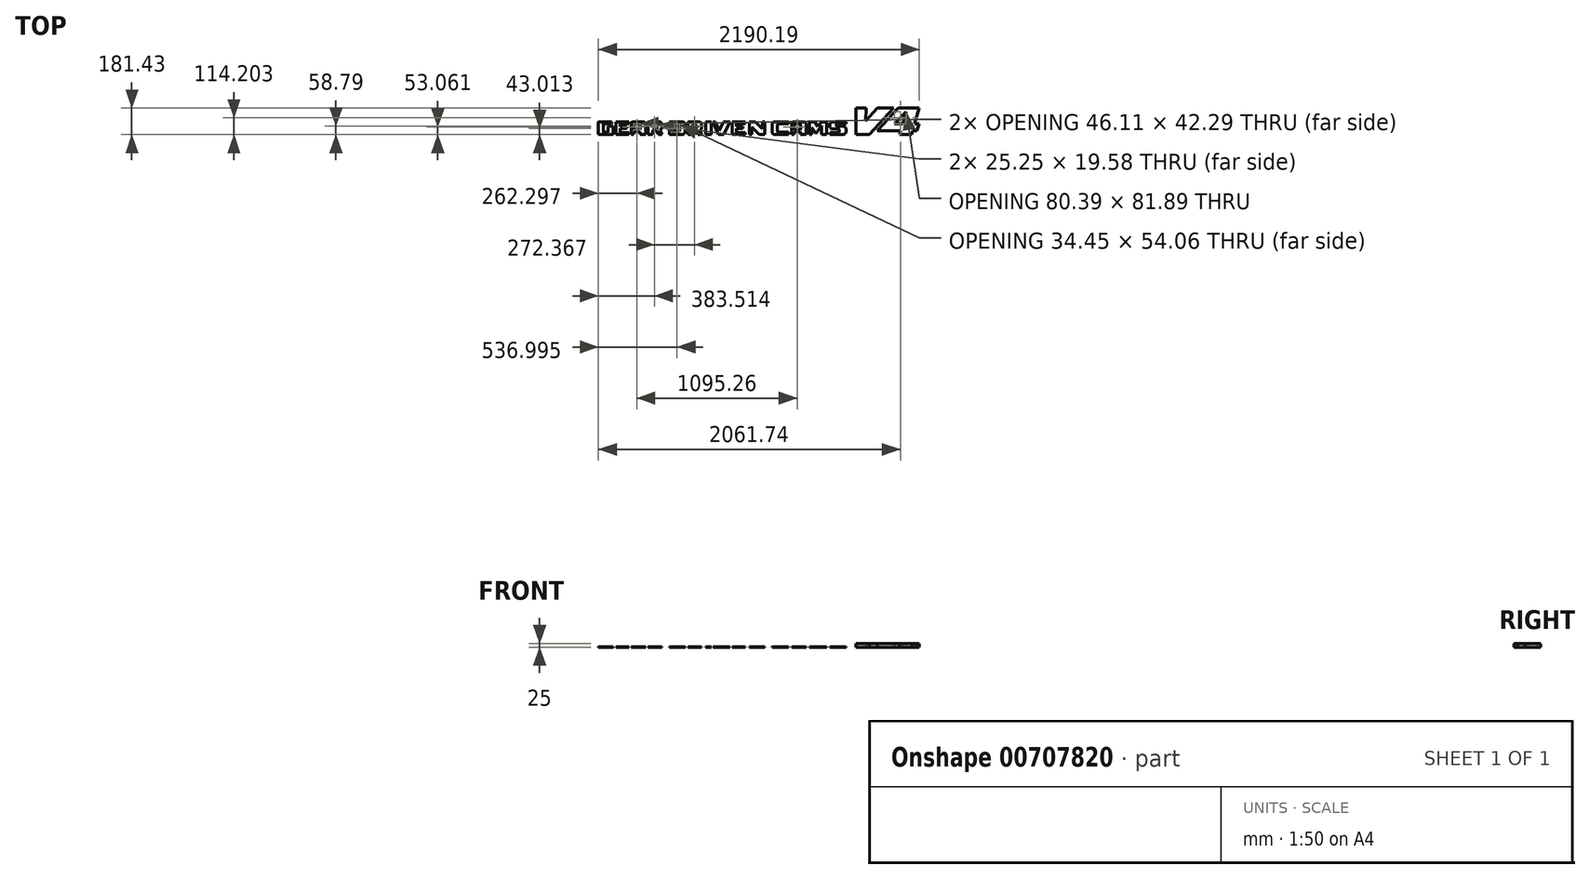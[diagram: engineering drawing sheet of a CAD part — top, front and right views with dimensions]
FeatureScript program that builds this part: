
annotation { "Feature Type Name" : "Feature", "Feature Type Description" : "" }
export const myFeature = defineFeature(function(context is Context, id is Id, definition is map)
    precondition{}
    {
        {
            var Q0;
            Q0=qCreatedBy(makeId("Top.planeOp"),FACE);
            var sketch = newSketch(context, id + "F0", { "sketchPlane" : qUnion([Q0])});
            skLineSegment(sketch, "E0", {"start": v(710.09, 395.52) * mm, "end": v(780, 395.52) * mm});
            skLineSegment(sketch, "E1", {"start": v(710.56, 214.09) * mm, "end": v(803.68, 214.09) * mm});
            skLineSegment(sketch, "E2", {"start": v(1092.02, 214.09) * mm, "end": v(1099.14, 239.05) * mm});
            skLineSegment(sketch, "E3", {"start": v(710.09, 395.52) * mm, "end": v(710.56, 214.09) * mm});
            skLineSegment(sketch, "E4", {"start": v(780, 395.52) * mm, "end": v(779.12, 307.5) * mm});
            skLineSegment(sketch, "E5", {"start": v(779.12, 307.5) * mm, "end": v(856.18, 395.52) * mm});
            skLineSegment(sketch, "E6", {"start": v(970.25, 395.52) * mm, "end": v(803.68, 214.09) * mm});
            skLineSegment(sketch, "E7", {"start": v(1000.95, 395.52) * mm, "end": v(857.3, 239.05) * mm});
            skLineSegment(sketch, "E8", {"start": v(1009.44, 214.09) * mm, "end": v(1016.85, 239.05) * mm});
            skLineSegment(sketch, "E9", {"start": v(975.1, 287.35) * mm, "end": v(1031.19, 287.35) * mm});
            skLineSegment(sketch, "E10", {"start": v(1142.08, 287.35) * mm, "end": v(1128.3, 239.05) * mm});
            skLineSegment(sketch, "E11", {"start": v(1128.3, 239.05) * mm, "end": v(1099.14, 239.05) * mm});
            skLineSegment(sketch, "E12.trimOffspring", {"start": v(856.18, 395.52) * mm, "end": v(970.25, 395.52) * mm});
            skLineSegment(sketch, "E13.trimOffspring", {"start": v(1009.44, 214.09) * mm, "end": v(1092.02, 214.09) * mm});
            skLineSegment(sketch, "E14.trimOffspring", {"start": v(1016.85, 239.05) * mm, "end": v(857.3, 239.05) * mm});
            skLineSegment(sketch, "E15.trimOffspring", {"start": v(1112.9, 287.35) * mm, "end": v(1142.08, 287.35) * mm});
            skLineSegment(sketch, "E16.trimOffspring", {"start": v(1031.19, 287.35) * mm, "end": v(1055.5, 369.24) * mm});
            skLineSegment(sketch, "E17.trimOffspring", {"start": v(1055.5, 369.24) * mm, "end": v(975.1, 287.35) * mm});
            skLineSegment(sketch, "E18.trimOffspring", {"start": v(1000.95, 395.52) * mm, "end": v(1151.02, 395.52) * mm});
            skLineSegment(sketch, "E19.trimOffspring", {"start": v(1112.9, 287.35) * mm, "end": v(1143.75, 395.52) * mm});
            skSolve(sketch);
        }
        {
            var Q0;
            Q0=makeQuery(id+"F0.imprint","IMPRINT",FACE,{"disambiguationData":[TD([[makeQuery(id+"F0.imprint","IMPRINT",EDGE,{"derivedFrom":sQuery(id+"F0.wireOp",EDGE,"E0")}),-1.0]])]});
            var Q1;
            Q1=makeQuery(id+"F0.imprint","IMPRINT",FACE,{"disambiguationData":[TD([[makeQuery(id+"F0.imprint","IMPRINT",EDGE,{"derivedFrom":sQuery(id+"F0.wireOp",EDGE,"E2")}),1.0]])]});
            extrude(context, id + "F1", {"entities" : qUnion([Q0, Q1]), "depth" : 25 * mm, "offsetDistance" : 25 * mm});
        }
        {
            var Q0;
            Q0=qCreatedBy(makeId("Top.planeOp"),FACE);
            var sketch = newSketch(context, id + "F2", { "sketchPlane" : qUnion([Q0])});
            skLineSegment(sketch, "E20", {"start": v(-1041.44, 302.21) * mm, "end": v(-955.7, 302.21) * mm});
            skLineSegment(sketch, "E21.0", {"start": v(-1041.44, 214.35) * mm, "end": v(-949.8, 214.35) * mm});
            skLineSegment(sketch, "E22", {"start": v(-1046.44, 219.35) * mm, "end": v(-1046.44, 297.21) * mm});
            skLineSegment(sketch, "E23", {"start": v(-1013.6, 236.44) * mm, "end": v(-1013.6, 283.53) * mm});
            skLineSegment(sketch, "E24", {"start": v(-979.78, 236.44) * mm, "end": v(-979.78, 270.86) * mm});
            skLineSegment(sketch, "E25", {"start": v(-944.8, 219.35) * mm, "end": v(-944.8, 270.86) * mm});
            skLineSegment(sketch, "E26", {"start": v(-925.97, 214.35) * mm, "end": v(-925.97, 302.21) * mm});
            skLineSegment(sketch, "E27", {"start": v(-897.14, 228.92) * mm, "end": v(-897.14, 255.43) * mm});
            skLineSegment(sketch, "E28", {"start": v(-852.65, 255.43) * mm, "end": v(-852.65, 269.68) * mm});
            skLineSegment(sketch, "E29", {"start": v(-838.3, 214.35) * mm, "end": v(-838.3, 228.92) * mm});
            skLineSegment(sketch, "E30", {"start": v(-822.44, 214.35) * mm, "end": v(-822.44, 289.99) * mm});
            skLineSegment(sketch, "E31", {"start": v(-807.2, 214.35) * mm, "end": v(-807.2, 233.5) * mm});
            skLineSegment(sketch, "E32", {"start": v(-761.09, 214.21) * mm, "end": v(-761.09, 233.5) * mm});
            skLineSegment(sketch, "E33", {"start": v(-723.62, 214.35) * mm, "end": v(-723.62, 283.68) * mm});
            skLineSegment(sketch, "E34", {"start": v(-706.35, 214.35) * mm, "end": v(-706.35, 302.21) * mm});
            skLineSegment(sketch, "E35", {"start": v(-675.55, 214.35) * mm, "end": v(-675.55, 243.5) * mm});
            skLineSegment(sketch, "E36", {"start": v(-613.77, 264.76) * mm, "end": v(-613.77, 284.75) * mm});
            skLineSegment(sketch, "E37", {"start": v(-1008.6, 231.44) * mm, "end": v(-984.78, 231.44) * mm});
            skLineSegment(sketch, "E38", {"start": v(-955.7, 288.53) * mm, "end": v(-955.7, 302.21) * mm});
            skLineSegment(sketch, "E39", {"start": v(-955.7, 288.53) * mm, "end": v(-1008.6, 288.53) * mm});
            skLineSegment(sketch, "E40", {"start": v(-944.8, 270.86) * mm, "end": v(-979.78, 270.86) * mm});
            skLineSegment(sketch, "E41", {"start": v(-838.3, 287.94) * mm, "end": v(-897.14, 287.94) * mm});
            skLineSegment(sketch, "E42", {"start": v(-852.65, 269.68) * mm, "end": v(-897.14, 269.68) * mm});
            skLineSegment(sketch, "E43", {"start": v(-852.65, 255.43) * mm, "end": v(-897.14, 255.43) * mm});
            skLineSegment(sketch, "E44", {"start": v(-838.3, 228.92) * mm, "end": v(-897.14, 228.92) * mm});
            skLineSegment(sketch, "E45.trimOffspring", {"start": v(-897.14, 269.68) * mm, "end": v(-897.14, 287.94) * mm});
            skLineSegment(sketch, "E46.trimOffspring", {"start": v(-838.3, 287.94) * mm, "end": v(-838.3, 302.21) * mm});
            skLineSegment(sketch, "E47", {"start": v(-761.09, 233.5) * mm, "end": v(-807.2, 233.5) * mm});
            skLineSegment(sketch, "E48", {"start": v(-807.2, 246) * mm, "end": v(-761.09, 246) * mm});
            skLineSegment(sketch, "E49", {"start": v(-797.2, 288.3) * mm, "end": v(-771.09, 288.3) * mm});
            skLineSegment(sketch, "E50.trimOffspring", {"start": v(-761.09, 246) * mm, "end": v(-761.09, 278.3) * mm});
            skLineSegment(sketch, "E51.trimOffspring", {"start": v(-807.2, 246) * mm, "end": v(-807.2, 278.3) * mm});
            skLineSegment(sketch, "E52", {"start": v(-675.55, 243.5) * mm, "end": v(-650.3, 243.5) * mm});
            skLineSegment(sketch, "E53", {"start": v(-650.3, 243.5) * mm, "end": v(-638.77, 214.35) * mm});
            skLineSegment(sketch, "E54.bottom", {"start": v(-675.55, 263.09) * mm, "end": v(-650.3, 263.09) * mm});
            skLineSegment(sketch, "E54.top", {"start": v(-675.55, 282.67) * mm, "end": v(-650.3, 282.67) * mm});
            skLineSegment(sketch, "E54.left", {"start": v(-675.55, 263.09) * mm, "end": v(-675.55, 282.67) * mm});
            skLineSegment(sketch, "E54.right", {"start": v(-650.3, 263.09) * mm, "end": v(-650.3, 282.67) * mm});
            skLineSegment(sketch, "E55", {"start": v(-613.77, 214.35) * mm, "end": v(-625.3, 243.5) * mm});
            skArc(sketch, "E56", {"start": v(-613.77, 284.75) * mm, "mid": v(-620.33, 297.33) * mm, "end": v(-633.64, 302.21) * mm});
            skArc(sketch, "E57", {"start": v(-625.3, 243.5) * mm, "mid": v(-616.69, 252.58) * mm, "end": v(-613.77, 264.76) * mm});
            skPoint(sketch, "E58.visualSharp", {"position": v(-1013.6, 231.44) * mm});
            skArc(sketch, "E58.filletArc", {"start": v(-1013.6, 236.44) * mm, "mid": v(-1012.14, 232.9) * mm, "end": v(-1008.6, 231.44) * mm});
            skPoint(sketch, "E59.visualSharp", {"position": v(-979.78, 231.44) * mm});
            skArc(sketch, "E59.filletArc", {"start": v(-984.78, 231.44) * mm, "mid": v(-981.25, 232.9) * mm, "end": v(-979.78, 236.44) * mm});
            skPoint(sketch, "E60.visualSharp", {"position": v(-1013.6, 288.53) * mm});
            skArc(sketch, "E60.filletArc", {"start": v(-1008.6, 288.53) * mm, "mid": v(-1012.14, 287.07) * mm, "end": v(-1013.6, 283.53) * mm});
            skLineSegment(sketch, "E61.trimOffspring", {"start": v(-925.97, 302.21) * mm, "end": v(-838.3, 302.21) * mm});
            skLineSegment(sketch, "E62.trimOffspring", {"start": v(-925.97, 214.35) * mm, "end": v(-838.3, 214.35) * mm});
            skPoint(sketch, "E63.visualSharp", {"position": v(-1046.44, 302.21) * mm});
            skArc(sketch, "E63.filletArc", {"start": v(-1041.44, 302.21) * mm, "mid": v(-1044.97, 300.75) * mm, "end": v(-1046.44, 297.21) * mm});
            skPoint(sketch, "E64.visualSharp", {"position": v(-1046.44, 214.35) * mm});
            skArc(sketch, "E64.filletArc", {"start": v(-1046.44, 219.35) * mm, "mid": v(-1044.97, 215.8) * mm, "end": v(-1041.44, 214.35) * mm});
            skPoint(sketch, "E65.visualSharp", {"position": v(-944.8, 214.35) * mm});
            skArc(sketch, "E65.filletArc", {"start": v(-949.8, 214.35) * mm, "mid": v(-946.26, 215.8) * mm, "end": v(-944.8, 219.35) * mm});
            skLineSegment(sketch, "E66.trimOffspring", {"start": v(-807.96, 302.21) * mm, "end": v(-742.83, 302.21) * mm});
            skLineSegment(sketch, "E67.trimOffspring", {"start": v(-822.44, 214.35) * mm, "end": v(-807.2, 214.35) * mm});
            skLineSegment(sketch, "E68.trimOffspring", {"start": v(-706.35, 214.35) * mm, "end": v(-675.55, 214.35) * mm});
            skLineSegment(sketch, "E69.trimOffspring", {"start": v(-706.35, 302.21) * mm, "end": v(-632.95, 302.21) * mm});
            skLineSegment(sketch, "E70.trimOffspring", {"start": v(-638.77, 214.35) * mm, "end": v(-613.77, 214.35) * mm});
            skArc(sketch, "E71", {"start": v(-807.96, 302.21) * mm, "mid": v(-817.4, 298.71) * mm, "end": v(-822.44, 289.99) * mm});
            skArc(sketch, "E72", {"start": v(-723.62, 283.68) * mm, "mid": v(-729.82, 296.96) * mm, "end": v(-743.5, 302.21) * mm});
            skPoint(sketch, "E73.visualSharp", {"position": v(-807.2, 288.3) * mm});
            skArc(sketch, "E73.filletArc", {"start": v(-797.2, 288.3) * mm, "mid": v(-804.27, 285.37) * mm, "end": v(-807.2, 278.3) * mm});
            skPoint(sketch, "E74.visualSharp", {"position": v(-761.09, 288.3) * mm});
            skArc(sketch, "E74.filletArc", {"start": v(-761.09, 278.3) * mm, "mid": v(-764.02, 285.37) * mm, "end": v(-771.09, 288.3) * mm});
            skLineSegment(sketch, "E75.trimOffspring", {"start": v(-761.09, 214.35) * mm, "end": v(-723.62, 214.35) * mm});
            skLineSegment(sketch, "E76", {"start": v(-562.57, 214.35) * mm, "end": v(-562.57, 302.21) * mm});
            skLineSegment(sketch, "E77", {"start": v(-526.67, 230.07) * mm, "end": v(-526.67, 284.13) * mm});
            skLineSegment(sketch, "E78", {"start": v(-492.22, 242.07) * mm, "end": v(-492.22, 272.13) * mm});
            skLineSegment(sketch, "E79", {"start": v(-454.92, 233.35) * mm, "end": v(-454.92, 283.21) * mm});
            skLineSegment(sketch, "E80", {"start": v(-526.67, 230.07) * mm, "end": v(-504.22, 230.07) * mm});
            skLineSegment(sketch, "E81", {"start": v(-526.67, 284.13) * mm, "end": v(-504.22, 284.13) * mm});
            skLineSegment(sketch, "E82", {"start": v(-433.98, 214.35) * mm, "end": v(-433.98, 302.21) * mm});
            skLineSegment(sketch, "E83", {"start": v(-403.18, 214.35) * mm, "end": v(-403.18, 243.5) * mm});
            skLineSegment(sketch, "E84", {"start": v(-341.4, 264.76) * mm, "end": v(-341.4, 284.75) * mm});
            skLineSegment(sketch, "E85", {"start": v(-403.18, 243.5) * mm, "end": v(-377.94, 243.5) * mm});
            skLineSegment(sketch, "E86", {"start": v(-377.94, 243.5) * mm, "end": v(-366.4, 214.35) * mm});
            skLineSegment(sketch, "E87.bottom", {"start": v(-403.18, 263.09) * mm, "end": v(-377.94, 263.09) * mm});
            skLineSegment(sketch, "E87.top", {"start": v(-403.18, 282.67) * mm, "end": v(-377.94, 282.67) * mm});
            skLineSegment(sketch, "E87.left", {"start": v(-403.18, 263.09) * mm, "end": v(-403.18, 282.67) * mm});
            skLineSegment(sketch, "E87.right", {"start": v(-377.94, 263.09) * mm, "end": v(-377.94, 282.67) * mm});
            skLineSegment(sketch, "E88", {"start": v(-341.4, 214.35) * mm, "end": v(-352.94, 243.5) * mm});
            skArc(sketch, "E89", {"start": v(-341.4, 284.75) * mm, "mid": v(-347.96, 297.33) * mm, "end": v(-361.27, 302.21) * mm});
            skArc(sketch, "E90", {"start": v(-352.94, 243.5) * mm, "mid": v(-344.32, 252.58) * mm, "end": v(-341.4, 264.76) * mm});
            skLineSegment(sketch, "E91.trimOffspring", {"start": v(-433.98, 214.35) * mm, "end": v(-403.18, 214.35) * mm});
            skLineSegment(sketch, "E92", {"start": v(-313.98, 214.35) * mm, "end": v(-313.98, 302.21) * mm});
            skLineSegment(sketch, "E93", {"start": v(-276.13, 214.35) * mm, "end": v(-276.13, 302.21) * mm});
            skLineSegment(sketch, "E94", {"start": v(-264.3, 302.21) * mm, "end": v(-229.62, 214.35) * mm});
            skLineSegment(sketch, "E95", {"start": v(-245.97, 302.21) * mm, "end": v(-221.92, 241.29) * mm});
            skLineSegment(sketch, "E96", {"start": v(-221.92, 241.29) * mm, "end": v(-192.95, 302.21) * mm});
            skLineSegment(sketch, "E97", {"start": v(-189.49, 214.35) * mm, "end": v(-147.71, 302.21) * mm});
            skLineSegment(sketch, "E98", {"start": v(-132.31, 214.35) * mm, "end": v(-132.31, 302.21) * mm});
            skLineSegment(sketch, "E99", {"start": v(-103.49, 228.92) * mm, "end": v(-103.49, 255.43) * mm});
            skLineSegment(sketch, "E100", {"start": v(-59, 255.43) * mm, "end": v(-59, 269.68) * mm});
            skLineSegment(sketch, "E101", {"start": v(-44.64, 214.35) * mm, "end": v(-44.64, 228.92) * mm});
            skLineSegment(sketch, "E102", {"start": v(-44.64, 287.94) * mm, "end": v(-103.49, 287.94) * mm});
            skLineSegment(sketch, "E103", {"start": v(-59, 269.68) * mm, "end": v(-103.49, 269.68) * mm});
            skLineSegment(sketch, "E104", {"start": v(-59, 255.43) * mm, "end": v(-103.49, 255.43) * mm});
            skLineSegment(sketch, "E105", {"start": v(-44.64, 228.92) * mm, "end": v(-103.49, 228.92) * mm});
            skLineSegment(sketch, "E106.trimOffspring", {"start": v(-103.49, 269.68) * mm, "end": v(-103.49, 287.94) * mm});
            skLineSegment(sketch, "E107.trimOffspring", {"start": v(-44.64, 287.94) * mm, "end": v(-44.64, 302.21) * mm});
            skLineSegment(sketch, "E108.trimOffspring", {"start": v(-132.31, 302.21) * mm, "end": v(-44.64, 302.21) * mm});
            skLineSegment(sketch, "E109.trimOffspring", {"start": v(-132.31, 214.35) * mm, "end": v(-44.64, 214.35) * mm});
            skLineSegment(sketch, "E110", {"start": v(-17, 214.35) * mm, "end": v(-17, 302.21) * mm});
            skLineSegment(sketch, "E111", {"start": v(0, 214.35) * mm, "end": v(0, 266.45) * mm});
            skLineSegment(sketch, "E112", {"start": v(72.6, 253.49) * mm, "end": v(72.6, 302.21) * mm});
            skLineSegment(sketch, "E113", {"start": v(89.95, 214.35) * mm, "end": v(89.95, 302.21) * mm});
            skLineSegment(sketch, "E114", {"start": v(25.32, 302.21) * mm, "end": v(72.6, 253.49) * mm});
            skLineSegment(sketch, "E115", {"start": v(0, 266.45) * mm, "end": v(50.55, 214.35) * mm});
            skLineSegment(sketch, "E116", {"start": v(138.96, 233.35) * mm, "end": v(138.96, 283.21) * mm});
            skLineSegment(sketch, "E117", {"start": v(174.7, 241.36) * mm, "end": v(174.7, 274.7) * mm});
            skLineSegment(sketch, "E118", {"start": v(252.03, 214.35) * mm, "end": v(252.03, 229.36) * mm});
            skLineSegment(sketch, "E119", {"start": v(392.53, 214.35) * mm, "end": v(392.53, 302.21) * mm});
            skLineSegment(sketch, "E120", {"start": v(410.35, 214.35) * mm, "end": v(410.35, 262.98) * mm});
            skLineSegment(sketch, "E121", {"start": v(475.18, 214.35) * mm, "end": v(475.49, 273.97) * mm});
            skLineSegment(sketch, "E122", {"start": v(510.56, 214.35) * mm, "end": v(510.56, 302.21) * mm});
            skLineSegment(sketch, "E123", {"start": v(533.94, 214.35) * mm, "end": v(533.94, 228.78) * mm});
            skLineSegment(sketch, "E124", {"start": v(643.75, 233.35) * mm, "end": v(643.75, 251.93) * mm});
            skLineSegment(sketch, "E125", {"start": v(272.81, 214.35) * mm, "end": v(272.81, 289.99) * mm});
            skLineSegment(sketch, "E126", {"start": v(288.06, 214.35) * mm, "end": v(288.06, 233.5) * mm});
            skLineSegment(sketch, "E127", {"start": v(334.17, 214.21) * mm, "end": v(334.17, 233.5) * mm});
            skLineSegment(sketch, "E128", {"start": v(371.64, 214.35) * mm, "end": v(371.64, 283.68) * mm});
            skLineSegment(sketch, "E129", {"start": v(334.17, 233.5) * mm, "end": v(288.06, 233.5) * mm});
            skLineSegment(sketch, "E130", {"start": v(288.06, 246) * mm, "end": v(334.17, 246) * mm});
            skLineSegment(sketch, "E131", {"start": v(298.06, 288.3) * mm, "end": v(324.17, 288.3) * mm});
            skLineSegment(sketch, "E132.trimOffspring", {"start": v(334.17, 246) * mm, "end": v(334.17, 278.3) * mm});
            skLineSegment(sketch, "E133.trimOffspring", {"start": v(288.06, 246) * mm, "end": v(288.06, 278.3) * mm});
            skLineSegment(sketch, "E134.trimOffspring", {"start": v(287.3, 302.21) * mm, "end": v(352.42, 302.21) * mm});
            skLineSegment(sketch, "E135.trimOffspring", {"start": v(272.81, 214.35) * mm, "end": v(288.06, 214.35) * mm});
            skArc(sketch, "E136", {"start": v(287.3, 302.21) * mm, "mid": v(277.85, 298.71) * mm, "end": v(272.81, 289.99) * mm});
            skArc(sketch, "E137", {"start": v(371.64, 283.68) * mm, "mid": v(365.43, 296.96) * mm, "end": v(351.75, 302.21) * mm});
            skPoint(sketch, "E138.visualSharp", {"position": v(288.06, 288.3) * mm});
            skArc(sketch, "E138.filletArc", {"start": v(298.06, 288.3) * mm, "mid": v(290.99, 285.37) * mm, "end": v(288.06, 278.3) * mm});
            skPoint(sketch, "E139.visualSharp", {"position": v(334.17, 288.3) * mm});
            skArc(sketch, "E139.filletArc", {"start": v(334.17, 278.3) * mm, "mid": v(331.24, 285.37) * mm, "end": v(324.17, 288.3) * mm});
            skLineSegment(sketch, "E140.trimOffspring", {"start": v(334.17, 214.35) * mm, "end": v(371.64, 214.35) * mm});
            skLineSegment(sketch, "E141", {"start": v(186.7, 286.7) * mm, "end": v(252.03, 286.7) * mm});
            skLineSegment(sketch, "E142", {"start": v(186.7, 229.36) * mm, "end": v(252.03, 229.36) * mm});
            skLineSegment(sketch, "E143", {"start": v(433.34, 302.21) * mm, "end": v(451.68, 269.92) * mm});
            skLineSegment(sketch, "E144", {"start": v(475.63, 302.21) * mm, "end": v(451.68, 269.92) * mm});
            skLineSegment(sketch, "E145", {"start": v(410.35, 262.98) * mm, "end": v(437.87, 221.76) * mm});
            skLineSegment(sketch, "E146", {"start": v(437.87, 221.76) * mm, "end": v(475.49, 273.97) * mm});
            skLineSegment(sketch, "E147.trimOffspring", {"start": v(475.63, 302.21) * mm, "end": v(510.56, 302.21) * mm});
            skLineSegment(sketch, "E148.trimOffspring", {"start": v(475.18, 214.35) * mm, "end": v(510.56, 214.35) * mm});
            skLineSegment(sketch, "E149.trimOffspring", {"start": v(-433.98, 302.21) * mm, "end": v(-360.58, 302.21) * mm});
            skLineSegment(sketch, "E150.trimOffspring", {"start": v(-562.57, 214.35) * mm, "end": v(-473.92, 214.35) * mm});
            skLineSegment(sketch, "E151.trimOffspring", {"start": v(-562.57, 302.21) * mm, "end": v(-473.92, 302.21) * mm});
            skPoint(sketch, "E152.visualSharp", {"position": v(-454.92, 302.21) * mm});
            skArc(sketch, "E152.filletArc", {"start": v(-454.92, 283.21) * mm, "mid": v(-460.48, 296.65) * mm, "end": v(-473.92, 302.21) * mm});
            skPoint(sketch, "E153.visualSharp", {"position": v(-454.92, 214.35) * mm});
            skArc(sketch, "E153.filletArc", {"start": v(-473.92, 214.35) * mm, "mid": v(-460.48, 219.91) * mm, "end": v(-454.92, 233.35) * mm});
            skPoint(sketch, "E154.visualSharp", {"position": v(-492.22, 284.13) * mm});
            skArc(sketch, "E154.filletArc", {"start": v(-492.22, 272.13) * mm, "mid": v(-495.73, 280.62) * mm, "end": v(-504.22, 284.13) * mm});
            skPoint(sketch, "E155.visualSharp", {"position": v(-492.22, 230.07) * mm});
            skArc(sketch, "E155.filletArc", {"start": v(-504.22, 230.07) * mm, "mid": v(-495.73, 233.59) * mm, "end": v(-492.22, 242.07) * mm});
            skLineSegment(sketch, "E156.trimOffspring", {"start": v(-313.98, 302.21) * mm, "end": v(-276.13, 302.21) * mm});
            skLineSegment(sketch, "E157.trimOffspring", {"start": v(-313.98, 214.35) * mm, "end": v(-276.13, 214.35) * mm});
            skLineSegment(sketch, "E158.trimOffspring", {"start": v(-366.4, 214.35) * mm, "end": v(-341.4, 214.35) * mm});
            skLineSegment(sketch, "E159.trimOffspring", {"start": v(-229.62, 214.35) * mm, "end": v(-189.49, 214.35) * mm});
            skLineSegment(sketch, "E160.trimOffspring", {"start": v(-264.3, 302.21) * mm, "end": v(-245.97, 302.21) * mm});
            skLineSegment(sketch, "E161.trimOffspring", {"start": v(-192.95, 302.21) * mm, "end": v(-147.71, 302.21) * mm});
            skLineSegment(sketch, "E162.trimOffspring", {"start": v(-17, 214.35) * mm, "end": v(0, 214.35) * mm});
            skLineSegment(sketch, "E163.trimOffspring", {"start": v(-17, 302.21) * mm, "end": v(25.32, 302.21) * mm});
            skLineSegment(sketch, "E164.trimOffspring", {"start": v(72.6, 302.21) * mm, "end": v(89.95, 302.21) * mm});
            skLineSegment(sketch, "E165.trimOffspring", {"start": v(50.55, 214.35) * mm, "end": v(89.95, 214.35) * mm});
            skLineSegment(sketch, "E166.trimOffspring", {"start": v(157.96, 302.21) * mm, "end": v(252.03, 302.21) * mm});
            skLineSegment(sketch, "E167.trimOffspring", {"start": v(157.96, 214.35) * mm, "end": v(252.03, 214.35) * mm});
            skLineSegment(sketch, "E168.trimOffspring", {"start": v(252.03, 286.7) * mm, "end": v(252.03, 302.21) * mm});
            skPoint(sketch, "E169.visualSharp", {"position": v(138.96, 302.21) * mm});
            skArc(sketch, "E169.filletArc", {"start": v(157.96, 302.21) * mm, "mid": v(144.52, 296.65) * mm, "end": v(138.96, 283.21) * mm});
            skPoint(sketch, "E170.visualSharp", {"position": v(138.96, 214.35) * mm});
            skArc(sketch, "E170.filletArc", {"start": v(138.96, 233.35) * mm, "mid": v(144.52, 219.91) * mm, "end": v(157.96, 214.35) * mm});
            skPoint(sketch, "E171.visualSharp", {"position": v(174.7, 286.7) * mm});
            skArc(sketch, "E171.filletArc", {"start": v(186.7, 286.7) * mm, "mid": v(178.21, 283.19) * mm, "end": v(174.7, 274.7) * mm});
            skPoint(sketch, "E172.visualSharp", {"position": v(174.7, 229.36) * mm});
            skArc(sketch, "E172.filletArc", {"start": v(174.7, 241.36) * mm, "mid": v(178.21, 232.87) * mm, "end": v(186.7, 229.36) * mm});
            skLineSegment(sketch, "E173", {"start": v(598.7, 233.78) * mm, "end": v(598.7, 247.08) * mm});
            skLineSegment(sketch, "E174", {"start": v(643.75, 287.49) * mm, "end": v(584.2, 287.49) * mm});
            skLineSegment(sketch, "E175", {"start": v(624.75, 270.93) * mm, "end": v(584.2, 270.93) * mm});
            skLineSegment(sketch, "E176", {"start": v(533.94, 228.78) * mm, "end": v(593.7, 228.78) * mm});
            skLineSegment(sketch, "E177", {"start": v(552.94, 252.08) * mm, "end": v(593.7, 252.08) * mm});
            skLineSegment(sketch, "E178.trimOffspring", {"start": v(579.2, 275.93) * mm, "end": v(579.2, 282.49) * mm});
            skLineSegment(sketch, "E179.trimOffspring", {"start": v(643.75, 287.49) * mm, "end": v(643.75, 302.21) * mm});
            skLineSegment(sketch, "E180.trimOffspring", {"start": v(533.94, 271.08) * mm, "end": v(533.94, 283.21) * mm});
            skPoint(sketch, "E181.orphan", {"position": v(598.7, 214.35) * mm});
            skLineSegment(sketch, "E182.trimOffspring", {"start": v(552.94, 302.21) * mm, "end": v(643.75, 302.21) * mm});
            skLineSegment(sketch, "E183.trimOffspring", {"start": v(533.94, 214.35) * mm, "end": v(624.75, 214.35) * mm});
            skLineSegment(sketch, "E184.trimOffspring", {"start": v(392.53, 214.35) * mm, "end": v(410.35, 214.35) * mm});
            skLineSegment(sketch, "E185.trimOffspring", {"start": v(392.53, 302.21) * mm, "end": v(433.34, 302.21) * mm});
            skPoint(sketch, "E186.visualSharp", {"position": v(533.94, 302.21) * mm});
            skArc(sketch, "E186.filletArc", {"start": v(552.94, 302.21) * mm, "mid": v(539.5, 296.65) * mm, "end": v(533.94, 283.21) * mm});
            skPoint(sketch, "E187.visualSharp", {"position": v(533.94, 252.08) * mm});
            skArc(sketch, "E187.filletArc", {"start": v(533.94, 271.08) * mm, "mid": v(539.5, 257.64) * mm, "end": v(552.94, 252.08) * mm});
            skPoint(sketch, "E188.visualSharp", {"position": v(643.75, 270.93) * mm});
            skArc(sketch, "E188.filletArc", {"start": v(643.75, 251.93) * mm, "mid": v(638.19, 265.37) * mm, "end": v(624.75, 270.93) * mm});
            skPoint(sketch, "E189.visualSharp", {"position": v(643.75, 214.35) * mm});
            skArc(sketch, "E189.filletArc", {"start": v(624.75, 214.35) * mm, "mid": v(638.19, 219.91) * mm, "end": v(643.75, 233.35) * mm});
            skPoint(sketch, "E190.visualSharp", {"position": v(579.2, 287.49) * mm});
            skArc(sketch, "E190.filletArc", {"start": v(584.2, 287.49) * mm, "mid": v(580.67, 286.02) * mm, "end": v(579.2, 282.49) * mm});
            skPoint(sketch, "E191.visualSharp", {"position": v(579.2, 270.93) * mm});
            skArc(sketch, "E191.filletArc", {"start": v(579.2, 275.93) * mm, "mid": v(580.67, 272.4) * mm, "end": v(584.2, 270.93) * mm});
            skPoint(sketch, "E192.visualSharp", {"position": v(598.7, 252.08) * mm});
            skArc(sketch, "E192.filletArc", {"start": v(598.7, 247.08) * mm, "mid": v(597.24, 250.61) * mm, "end": v(593.7, 252.08) * mm});
            skPoint(sketch, "E193.visualSharp", {"position": v(598.7, 228.78) * mm});
            skArc(sketch, "E193.filletArc", {"start": v(593.7, 228.78) * mm, "mid": v(597.24, 230.24) * mm, "end": v(598.7, 233.78) * mm});
            skSolve(sketch);
        }
        {
            var Q0;
            Q0=makeQuery(id+"F2.imprint","IMPRINT",FACE,{"disambiguationData":[TD([[makeQuery(id+"F2.imprint","IMPRINT",EDGE,{"derivedFrom":sQuery(id+"F2.wireOp",EDGE,"E20")}),-1.0]])]});
            var Q1;
            Q1=makeQuery(id+"F2.imprint","IMPRINT",FACE,{"disambiguationData":[TD([[makeQuery(id+"F2.imprint","IMPRINT",EDGE,{"derivedFrom":sQuery(id+"F2.wireOp",EDGE,"E26")}),-1.0]])]});
            var Q2;
            Q2=makeQuery(id+"F2.imprint","IMPRINT",FACE,{"disambiguationData":[TD([[makeQuery(id+"F2.imprint","IMPRINT",EDGE,{"derivedFrom":sQuery(id+"F2.wireOp",EDGE,"E30")}),-1.0]])]});
            var Q3;
            {var subQ0=sQuery(id+"F2.wireOp",EDGE,"E34");Q3=makeQuery(id+"F2.imprint","IMPRINT",FACE,{"disambiguationData":[TD([[makeQuery(id+"F2.imprint","IMPRINT",EDGE,{"derivedFrom":subQ0}),-1.0]])]});}
            var Q4;
            Q4=makeQuery(id+"F2.imprint","IMPRINT",FACE,{"disambiguationData":[TD([[makeQuery(id+"F2.imprint","IMPRINT",EDGE,{"derivedFrom":sQuery(id+"F2.wireOp",EDGE,"E76")}),-1.0]])]});
            var Q5;
            {var subQ0=sQuery(id+"F2.wireOp",EDGE,"E82");Q5=makeQuery(id+"F2.imprint","IMPRINT",FACE,{"disambiguationData":[TD([[makeQuery(id+"F2.imprint","IMPRINT",EDGE,{"derivedFrom":subQ0}),-1.0]])]});}
            var Q6;
            Q6=makeQuery(id+"F2.imprint","IMPRINT",FACE,{"disambiguationData":[TD([[makeQuery(id+"F2.imprint","IMPRINT",EDGE,{"derivedFrom":sQuery(id+"F2.wireOp",EDGE,"E92")}),-1.0]])]});
            var Q7;
            Q7=makeQuery(id+"F2.imprint","IMPRINT",FACE,{"disambiguationData":[TD([[makeQuery(id+"F2.imprint","IMPRINT",EDGE,{"derivedFrom":sQuery(id+"F2.wireOp",EDGE,"E94")}),1.0]])]});
            var Q8;
            Q8=makeQuery(id+"F2.imprint","IMPRINT",FACE,{"disambiguationData":[TD([[makeQuery(id+"F2.imprint","IMPRINT",EDGE,{"derivedFrom":sQuery(id+"F2.wireOp",EDGE,"E98")}),-1.0]])]});
            var Q9;
            Q9=makeQuery(id+"F2.imprint","IMPRINT",FACE,{"disambiguationData":[TD([[makeQuery(id+"F2.imprint","IMPRINT",EDGE,{"derivedFrom":sQuery(id+"F2.wireOp",EDGE,"E110")}),-1.0]])]});
            var Q10;
            Q10=makeQuery(id+"F2.imprint","IMPRINT",FACE,{"disambiguationData":[TD([[makeQuery(id+"F2.imprint","IMPRINT",EDGE,{"derivedFrom":sQuery(id+"F2.wireOp",EDGE,"E116")}),-1.0]])]});
            var Q11;
            Q11=makeQuery(id+"F2.imprint","IMPRINT",FACE,{"disambiguationData":[TD([[makeQuery(id+"F2.imprint","IMPRINT",EDGE,{"derivedFrom":sQuery(id+"F2.wireOp",EDGE,"E125")}),-1.0]])]});
            var Q12;
            Q12=makeQuery(id+"F2.imprint","IMPRINT",FACE,{"disambiguationData":[TD([[makeQuery(id+"F2.imprint","IMPRINT",EDGE,{"derivedFrom":sQuery(id+"F2.wireOp",EDGE,"E119")}),-1.0]])]});
            var Q13;
            Q13=makeQuery(id+"F2.imprint","IMPRINT",FACE,{"disambiguationData":[TD([[makeQuery(id+"F2.imprint","IMPRINT",EDGE,{"derivedFrom":sQuery(id+"F2.wireOp",EDGE,"E123")}),-1.0]])]});
            extrude(context, id + "F3", {"entities" : qUnion([Q0, Q1, Q2, Q3, Q4, Q5, Q6, Q7, Q8, Q9, Q10, Q11, Q12, Q13]), "depth" : 1 * mm, "offsetDistance" : 25 * mm});
        }
    });
